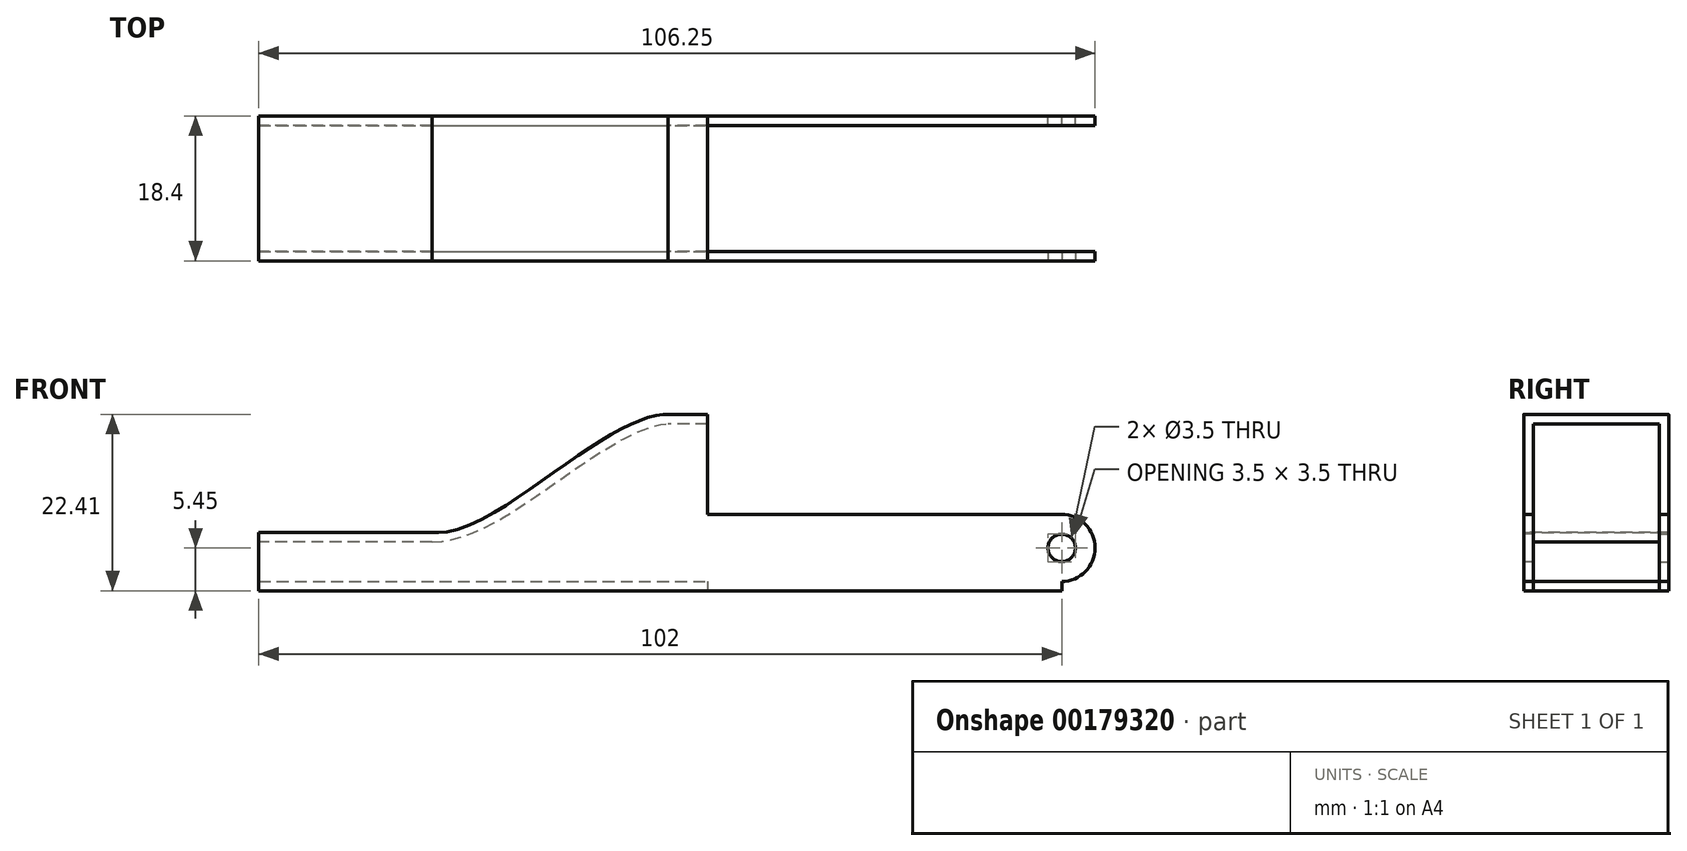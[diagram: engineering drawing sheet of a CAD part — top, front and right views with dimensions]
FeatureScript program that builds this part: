
annotation { "Feature Type Name" : "Feature", "Feature Type Description" : "" }
export const myFeature = defineFeature(function(context is Context, id is Id, definition is map)
    precondition{}
    {
        {
            var Q0;
            Q0=qCreatedBy(makeId("Front.planeOp"),FACE);
            var sketch = newSketch(context, id + "F0", { "sketchPlane" : qUnion([Q0])});
            skLineSegment(sketch, "E0.bottom", {"start": v(2.5, -10) * mm, "end": v(-2.5, -10) * mm});
            skLineSegment(sketch, "E0.top", {"start": v(2.5, 10) * mm, "end": v(-2.5, 10) * mm});
            skLineSegment(sketch, "E0.left", {"start": v(2.5, -10) * mm, "end": v(2.5, 10) * mm});
            skLineSegment(sketch, "E0.right", {"start": v(-2.5, -10) * mm, "end": v(-2.5, 10) * mm});
            skPoint(sketch, "E0.middle", {"position": v(0, 0) * mm});
            skLineSegment(sketch, "E1.bottom", {"start": v(-32.5, -10) * mm, "end": v(-54.5, -10) * mm});
            skLineSegment(sketch, "E1.top", {"start": v(-32.5, -5) * mm, "end": v(-54.5, -5) * mm});
            skLineSegment(sketch, "E1.left", {"start": v(-32.5, -10) * mm, "end": v(-32.5, -5) * mm});
            skLineSegment(sketch, "E1.right", {"start": v(-54.5, -10) * mm, "end": v(-54.5, -5) * mm});
            skLineSegment(sketch, "E2", {"start": v(-32.5, -10) * mm, "end": v(-2.5, -10) * mm});
            skLineSegment(sketch, "E3.bottom", {"start": v(2.5, -10) * mm, "end": v(47.5, -10) * mm});
            skLineSegment(sketch, "E3.top", {"start": v(2.5, -1.5) * mm, "end": v(47.5, -1.5) * mm});
            skLineSegment(sketch, "E3.left", {"start": v(2.5, -10) * mm, "end": v(2.5, -1.5) * mm});
            skLineSegment(sketch, "E3.right", {"start": v(47.5, -10) * mm, "end": v(47.5, -1.5) * mm});
            skArc(sketch, "E4", {"start": v(47.5, -10) * mm, "mid": v(51.75, -5.75) * mm, "end": v(47.5, -1.5) * mm});
            skFitSpline(sketch, "E5", {"points": [v(-32.5, -5) * mm, v(-16.82, 2.5) * mm, v(-2.5, 10) * mm], "startDerivative": vector(29, 0) * mm, "endDerivative": vector(21.74, 0) * mm});
            skLineSegment(sketch, "E6.0", {"start": v(2.5, 11.2) * mm, "end": v(-2.5, 11.2) * mm});
            skFitSpline(sketch, "E6.1", {"points": [v(-32.5, -3.8) * mm, v(-31.44, -3.8) * mm, v(-29.22, -3.4) * mm, v(-25.6, -1.82) * mm, v(-21.79, 0.5) * mm, v(-17.82, 3.26) * mm, v(-13.73, 6.12) * mm, v(-10.38, 8.27) * mm, v(-7.82, 9.66) * mm, v(-5.97, 10.49) * mm, v(-4.2, 11.05) * mm, v(-3.06, 11.2) * mm, v(-2.5, 11.2) * mm]});
            skLineSegment(sketch, "E6.2", {"start": v(-32.5, -3.8) * mm, "end": v(-54.5, -3.8) * mm});
            skLineSegment(sketch, "E7", {"start": v(-54.5, -3.8) * mm, "end": v(-54.5, -5) * mm});
            skLineSegment(sketch, "E8", {"start": v(2.5, 11.2) * mm, "end": v(2.5, 10) * mm});
            skLineSegment(sketch, "E9.0", {"start": v(2.5, -11.2) * mm, "end": v(-2.84, -11.2) * mm});
            skLineSegment(sketch, "E9.1", {"start": v(-32.84, -11.2) * mm, "end": v(-2.84, -11.2) * mm});
            skLineSegment(sketch, "E9.2", {"start": v(-32.84, -11.2) * mm, "end": v(-54.5, -11.2) * mm});
            skLineSegment(sketch, "E10", {"start": v(-54.5, -10) * mm, "end": v(-54.5, -11.2) * mm});
            skLineSegment(sketch, "E11", {"start": v(2.5, -10) * mm, "end": v(2.5, -11.2) * mm});
            skLineSegment(sketch, "E12.bottom", {"start": v(2.5, -10) * mm, "end": v(2.5, -10) * mm});
            skLineSegment(sketch, "E12.top", {"start": v(2.5, -11.2) * mm, "end": v(2.5, -11.2) * mm});
            skLineSegment(sketch, "E13.bottom", {"start": v(2.5, -11.2) * mm, "end": v(47.5, -11.2) * mm});
            skLineSegment(sketch, "E13.left", {"start": v(2.5, -11.2) * mm, "end": v(2.5, -10) * mm});
            skLineSegment(sketch, "E13.right", {"start": v(47.5, -11.2) * mm, "end": v(47.5, -10) * mm});
            skSolve(sketch);
        }
        {
            var Q0;
            Q0=makeQuery(id+"F0.imprint","IMPRINT",FACE,{"disambiguationData":[TD([[makeQuery(id+"F0.imprint","IMPRINT",EDGE,{"derivedFrom":sQuery(id+"F0.wireOp",EDGE,"E3.right")}),-1.0]])]});
            var Q1;
            Q1=makeQuery(id+"F0.imprint","IMPRINT",FACE,{"disambiguationData":[TD([[makeQuery(id+"F0.imprint","IMPRINT",EDGE,{"derivedFrom":sQuery(id+"F0.wireOp",EDGE,"E3.top")}),-1.0]])]});
            var Q2;
            Q2=makeQuery(id+"F0.imprint","IMPRINT",FACE,{"disambiguationData":[TD([[makeQuery(id+"F0.imprint","IMPRINT",EDGE,{"derivedFrom":sQuery(id+"F0.wireOp",EDGE,"E13.bottom")}),1.0]])]});
            var Q3;
            Q3=makeQuery(id+"F0.imprint","IMPRINT",FACE,{"disambiguationData":[TD([[makeQuery(id+"F0.imprint","IMPRINT",EDGE,{"derivedFrom":sQuery(id+"F0.wireOp",EDGE,"E0.right")}),1.0]])]});
            var Q4;
            Q4=makeQuery(id+"F0.imprint","IMPRINT",FACE,{"disambiguationData":[TD([[makeQuery(id+"F0.imprint","IMPRINT",EDGE,{"derivedFrom":sQuery(id+"F0.wireOp",EDGE,"E0.bottom")}),-1.0]])]});
            var Q5;
            Q5=makeQuery(id+"F0.imprint","IMPRINT",FACE,{"disambiguationData":[TD([[makeQuery(id+"F0.imprint","IMPRINT",EDGE,{"derivedFrom":sQuery(id+"F0.wireOp",EDGE,"E1.bottom")}),-1.0]])]});
            extrude(context, id + "F1", {"entities" : qUnion([Q0, Q1, Q2, Q3, Q4, Q5]), "depth" : 1.2 * mm});
        }
        {
            var Q0;
            Q0=makeQuery(id+"F0.imprint","IMPRINT",FACE,{"disambiguationData":[TD([[makeQuery(id+"F0.imprint","IMPRINT",EDGE,{"derivedFrom":sQuery(id+"F0.wireOp",EDGE,"E0.top")}),-1.0]])]});
            var Q1;
            Q1=makeQuery(id+"F0.imprint","IMPRINT",FACE,{"disambiguationData":[TD([[makeQuery(id+"F0.imprint","IMPRINT",EDGE,{"derivedFrom":sQuery(id+"F0.wireOp",EDGE,"E0.bottom")}),1.0]])]});
            extrude(context, id + "F2", {"entities" : qUnion([Q0, Q1]), "operationType" : NewBodyOperationType.ADD, "depth" : 9.2 * mm});
        }
        {
            var Q0;
            Q0=sQuery(id+"F0.wireOp",VERTEX,"E4.center");
            var Q1;
            Q1=makeQuery(id+"F1.opExtrude","SWEPT_BODY",BODY,{"disambiguationData":[OSD([sQuery(id+"F0.wireOp",EDGE,"E0.bottom"),sQuery(id+"F0.wireOp",EDGE,"E0.top"),sQuery(id+"F0.wireOp",EDGE,"E0.left"),sQuery(id+"F0.wireOp",EDGE,"E1.bottom"),sQuery(id+"F0.wireOp",EDGE,"E1.top"),sQuery(id+"F0.wireOp",EDGE,"E1.right"),sQuery(id+"F0.wireOp",EDGE,"E2"),sQuery(id+"F0.wireOp",EDGE,"E3.top"),sQuery(id+"F0.wireOp",EDGE,"E4"),sQuery(id+"F0.wireOp",EDGE,"E5"),sQuery(id+"F0.wireOp",EDGE,"E13.bottom"),sQuery(id+"F0.wireOp",EDGE,"E13.left"),sQuery(id+"F0.wireOp",EDGE,"E13.right")])]});
            hole(context, id + "F3", {"style" : HoleStyle.SIMPLE, "endStyle" : HoleEndStyle.THROUGH, "oppositeDirection" : true, "holeDiameter" : 3.5 * mm, "locations" : qUnion([Q0]), "scope" : qUnion([Q1]), "isTappedThrough" : true});
        }
        {
            var Q0;
            Q0=makeQuery(id+"F1.opExtrude","SWEPT_BODY",BODY,{"disambiguationData":[OSD([sQuery(id+"F0.wireOp",EDGE,"E0.bottom"),sQuery(id+"F0.wireOp",EDGE,"E0.top"),sQuery(id+"F0.wireOp",EDGE,"E0.left"),sQuery(id+"F0.wireOp",EDGE,"E1.bottom"),sQuery(id+"F0.wireOp",EDGE,"E1.top"),sQuery(id+"F0.wireOp",EDGE,"E1.right"),sQuery(id+"F0.wireOp",EDGE,"E2"),sQuery(id+"F0.wireOp",EDGE,"E3.top"),sQuery(id+"F0.wireOp",EDGE,"E4"),sQuery(id+"F0.wireOp",EDGE,"E5"),sQuery(id+"F0.wireOp",EDGE,"E13.bottom"),sQuery(id+"F0.wireOp",EDGE,"E13.left"),sQuery(id+"F0.wireOp",EDGE,"E13.right")])]});
            var Q1;
            Q1=makeQuery(id+"F2.opExtrude","CAP_FACE",FACE,{"disambiguationData":[OSD([sQuery(id+"F0.wireOp",EDGE,"E0.bottom"),sQuery(id+"F0.wireOp",EDGE,"E1.bottom"),sQuery(id+"F0.wireOp",EDGE,"E2"),sQuery(id+"F0.wireOp",EDGE,"E9.0"),sQuery(id+"F0.wireOp",EDGE,"E9.1"),sQuery(id+"F0.wireOp",EDGE,"E9.2"),sQuery(id+"F0.wireOp",EDGE,"E10"),sQuery(id+"F0.wireOp",EDGE,"E13.left")])],"isStart":false});
            mirror(context, id + "F4", {"operationType" : NewBodyOperationType.ADD, "entities" : qUnion([Q0]), "mirrorPlane" : qUnion([Q1])});
        }
    });
